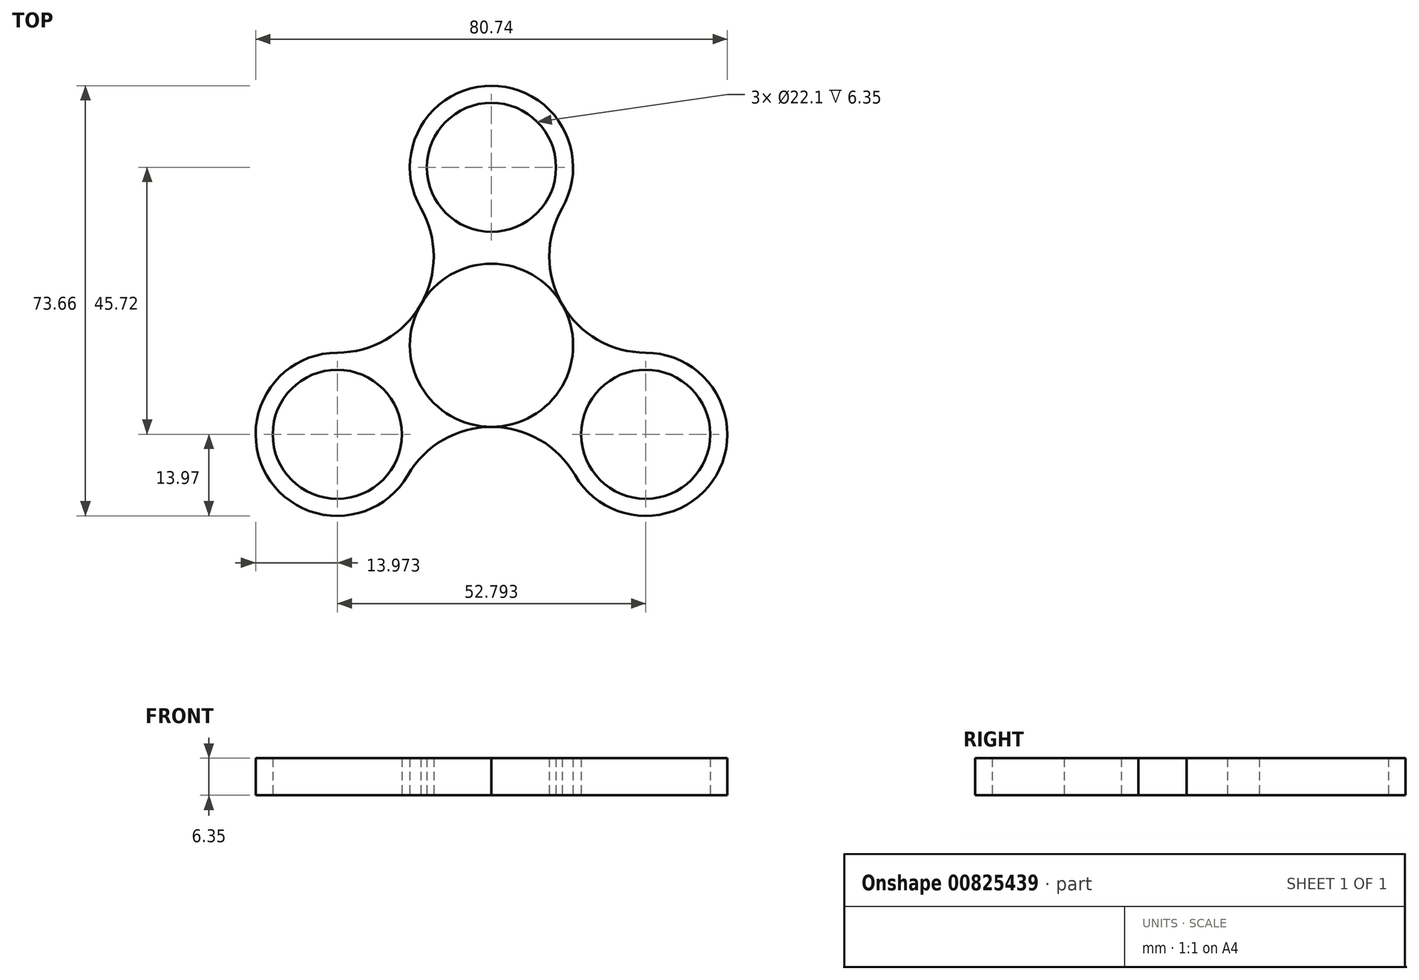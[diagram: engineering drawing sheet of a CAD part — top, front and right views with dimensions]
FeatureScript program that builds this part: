
annotation { "Feature Type Name" : "Feature", "Feature Type Description" : "" }
export const myFeature = defineFeature(function(context is Context, id is Id, definition is map)
    precondition{}
    {
        {
            var Q0;
            Q0=qCreatedBy(makeId("Top.planeOp"),FACE);
            var sketch = newSketch(context, id + "F0", { "sketchPlane" : qUnion([Q0])});
            skCircle(sketch, "E0", {"center": v(0, 0) * mm, "radius": 44.45 * mm});
            skCircle(sketch, "E1", {"center": v(0, 0) * mm, "radius": 11.05 * mm});
            skLineSegment(sketch, "E2", {"start": v(0, 0) * mm, "end": v(0, 30.48) * mm});
            skCircle(sketch, "E3", {"center": v(0, 30.48) * mm, "radius": 11.05 * mm});
            skCircle(sketch, "E4", {"center": v(0, 30.48) * mm, "radius": 13.97 * mm});
            skCircle(sketch, "E5.1.0", {"center": v(-26.4, -15.24) * mm, "radius": 13.97 * mm});
            skCircle(sketch, "E5.1.1", {"center": v(-26.4, -15.24) * mm, "radius": 11.05 * mm});
            skCircle(sketch, "E5.2.0", {"center": v(26.4, -15.24) * mm, "radius": 13.97 * mm});
            skCircle(sketch, "E5.2.1", {"center": v(26.4, -15.24) * mm, "radius": 11.05 * mm});
            skCircle(sketch, "E6", {"center": v(0, 0) * mm, "radius": 13.97 * mm});
            skLineSegment(sketch, "E7", {"start": v(0, 0) * mm, "end": v(-26.4, 15.24) * mm});
            skArc(sketch, "E8", {"start": v(-26.4, -1.27) * mm, "mid": v(-12.1, 6.98) * mm, "end": v(-12.1, 23.5) * mm});
            skArc(sketch, "E9.1.0", {"start": v(14.3, -22.23) * mm, "mid": v(0, -13.97) * mm, "end": v(-14.3, -22.22) * mm});
            skArc(sketch, "E9.2.0", {"start": v(12.1, 23.5) * mm, "mid": v(12.1, 6.99) * mm, "end": v(26.4, -1.27) * mm});
            skSolve(sketch);
        }
        {
            var Q0;
            Q0=makeQuery(id+"F0.imprint","IMPRINT",FACE,{"disambiguationData":[TD([[makeQuery(id+"F0.imprint","IMPRINT",EDGE,{"derivedFrom":sQuery(id+"F0.wireOp",EDGE,"E5.1.1")}),-1.0]])]});
            var Q1;
            {var subQ0=sQuery(id+"F0.wireOp",EDGE,"E8");var subQ1=sQuery(id+"F0.wireOp",EDGE,"E5.1.0");var subQ2=makeQuery(id+"F0.imprint","INTERSECT",VERTEX,{"derivedFrom":[subQ1,subQ0]});Q1=makeQuery(id+"F0.imprint","IMPRINT",FACE,{"disambiguationData":[TD([[makeQuery(id+"F0.imprint","IMPRINT",EDGE,{"disambiguationData":[TD([[subQ2,1.0]])],"derivedFrom":subQ1}),-1.0]])]});}
            var Q2;
            {var subQ0=sQuery(id+"F0.wireOp",EDGE,"E4");var subQ1=sQuery(id+"F0.wireOp",EDGE,"E2");var subQ2=makeQuery(id+"F0.imprint","INTERSECT",VERTEX,{"derivedFrom":[subQ1,subQ0]});Q2=makeQuery(id+"F0.imprint","IMPRINT",FACE,{"disambiguationData":[TD([[makeQuery(id+"F0.imprint","IMPRINT",EDGE,{"disambiguationData":[TD([[subQ2,1.0]])],"derivedFrom":subQ1}),1.0]])]});}
            var Q3;
            {var subQ0=sQuery(id+"F0.wireOp",EDGE,"E4");var subQ1=sQuery(id+"F0.wireOp",EDGE,"E2");var subQ2=makeQuery(id+"F0.imprint","INTERSECT",VERTEX,{"derivedFrom":[subQ1,subQ0]});Q3=makeQuery(id+"F0.imprint","IMPRINT",FACE,{"disambiguationData":[TD([[makeQuery(id+"F0.imprint","IMPRINT",EDGE,{"disambiguationData":[TD([[subQ2,1.0]])],"derivedFrom":subQ1}),-1.0]])]});}
            var Q4;
            Q4=makeQuery(id+"F0.imprint","IMPRINT",FACE,{"disambiguationData":[TD([[makeQuery(id+"F0.imprint","IMPRINT",EDGE,{"derivedFrom":sQuery(id+"F0.wireOp",EDGE,"E3")}),-1.0]])]});
            var Q5;
            Q5=makeQuery(id+"F0.imprint","IMPRINT",FACE,{"disambiguationData":[TD([[makeQuery(id+"F0.imprint","IMPRINT",EDGE,{"derivedFrom":sQuery(id+"F0.wireOp",EDGE,"E5.2.1")}),-1.0]])]});
            var Q6;
            {var subQ0=sQuery(id+"F0.wireOp",EDGE,"E9.1.0");var subQ1=sQuery(id+"F0.wireOp",EDGE,"E5.2.0");var subQ2=makeQuery(id+"F0.imprint","INTERSECT",VERTEX,{"derivedFrom":[subQ1,subQ0]});Q6=makeQuery(id+"F0.imprint","IMPRINT",FACE,{"disambiguationData":[TD([[makeQuery(id+"F0.imprint","IMPRINT",EDGE,{"disambiguationData":[TD([[subQ2,1.0]])],"derivedFrom":subQ1}),-1.0]])]});}
            extrude(context, id + "F1", {"entities" : qUnion([Q0, Q1, Q2, Q3, Q4, Q5, Q6]), "depth" : 6.35 * mm, "offsetDistance" : 25.4 * mm});
        }
    });
